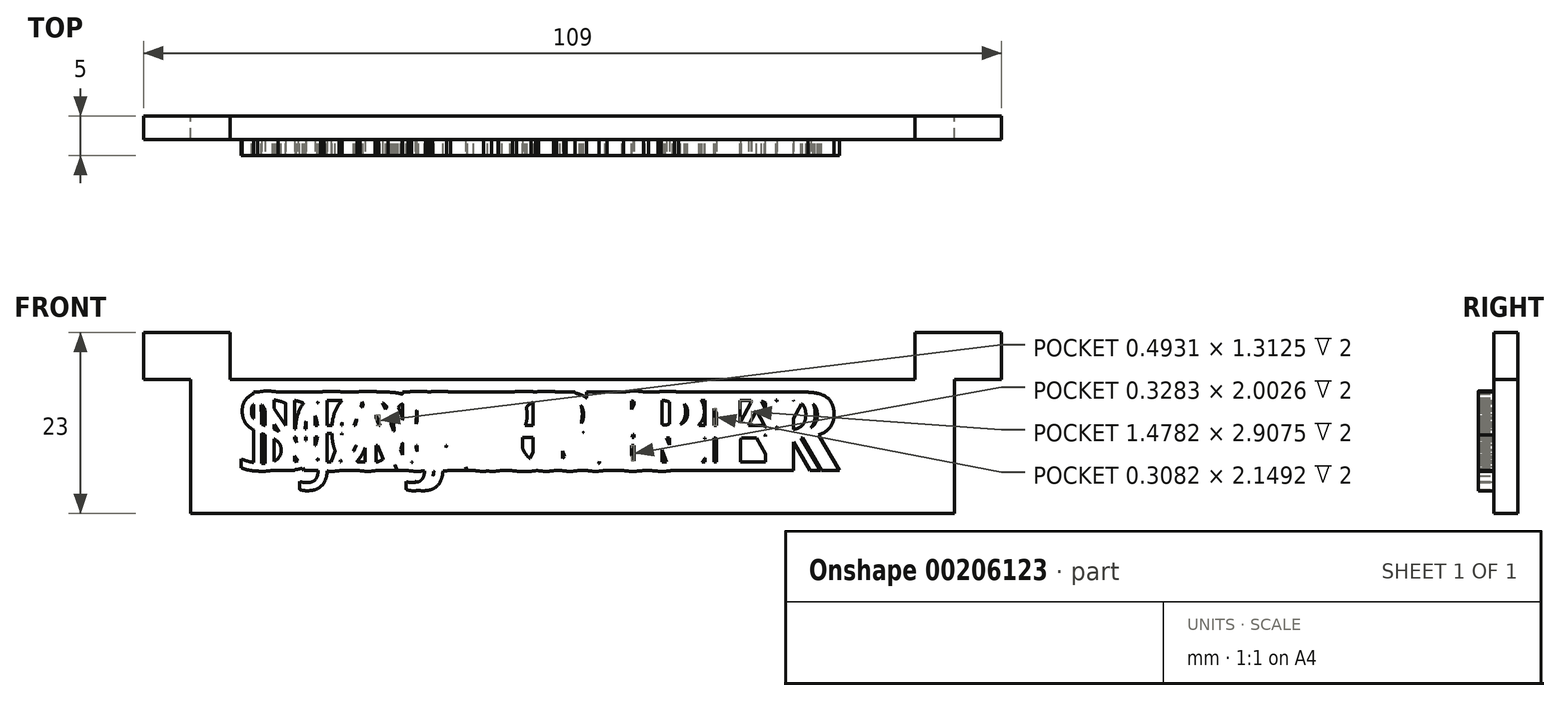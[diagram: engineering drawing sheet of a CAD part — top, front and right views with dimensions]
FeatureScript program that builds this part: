
annotation { "Feature Type Name" : "Feature", "Feature Type Description" : "" }
export const myFeature = defineFeature(function(context is Context, id is Id, definition is map)
    precondition{}
    {
        {
            var Q0;
            Q0=qCreatedBy(makeId("Front.planeOp"),FACE);
            var sketch = newSketch(context, id + "F0", { "sketchPlane" : qUnion([Q0])});
            skLineSegment(sketch, "E0.bottom", {"start": v(-51.5, 23) * mm, "end": v(-40.5, 23) * mm});
            skLineSegment(sketch, "E0.top", {"start": v(-45.5, 0) * mm, "end": v(51.5, 0) * mm});
            skLineSegment(sketch, "E0.left", {"start": v(-51.5, 23) * mm, "end": v(-51.5, 17) * mm});
            skLineSegment(sketch, "E0.right", {"start": v(57.5, 23) * mm, "end": v(57.5, 17) * mm});
            skLineSegment(sketch, "E1.top", {"start": v(-51.5, 17) * mm, "end": v(-45.5, 17) * mm});
            skLineSegment(sketch, "E1.right", {"start": v(-45.5, 0) * mm, "end": v(-45.5, 17) * mm});
            skLineSegment(sketch, "E2.bottom", {"start": v(-51.5, 23) * mm, "end": v(-40.5, 23) * mm, "construction": true});
            skLineSegment(sketch, "E2.top", {"start": v(-51.5, 17) * mm, "end": v(-40.5, 17) * mm, "construction": true});
            skLineSegment(sketch, "E2.left", {"start": v(-51.5, 23) * mm, "end": v(-51.5, 17) * mm, "construction": true});
            skLineSegment(sketch, "E2.right", {"start": v(-40.5, 23) * mm, "end": v(-40.5, 17) * mm, "construction": true});
            skLineSegment(sketch, "E3.top", {"start": v(-40.5, 17) * mm, "end": v(46.5, 17) * mm});
            skLineSegment(sketch, "E3.left", {"start": v(-40.5, 23) * mm, "end": v(-40.5, 17) * mm});
            skLineSegment(sketch, "E3.right", {"start": v(46.5, 23) * mm, "end": v(46.5, 17) * mm});
            skLineSegment(sketch, "E4.top", {"start": v(57.5, 17) * mm, "end": v(51.5, 17) * mm});
            skLineSegment(sketch, "E4.right", {"start": v(51.5, 0) * mm, "end": v(51.5, 17) * mm});
            skLineSegment(sketch, "E5.trimOffspring", {"start": v(46.5, 23) * mm, "end": v(57.5, 23) * mm});
            skSolve(sketch);
        }
        {
            var Q0;
            Q0=makeQuery(id+"F0.imprint","IMPRINT",FACE,{"disambiguationData":[TD([[makeQuery(id+"F0.imprint","IMPRINT",EDGE,{"derivedFrom":sQuery(id+"F0.wireOp",EDGE,"E0.bottom")}),-1.0]])]});
            extrude(context, id + "F1", {"entities" : qUnion([Q0]), "depth" : 3 * mm});
        }
        {
            var Q0;
            Q0=makeQuery(id+"F1.opExtrude","CAP_FACE",FACE,{"disambiguationData":[OSD([sQuery(id+"F0.wireOp",EDGE,"E0.bottom"),sQuery(id+"F0.wireOp",EDGE,"E0.top"),sQuery(id+"F0.wireOp",EDGE,"E0.left"),sQuery(id+"F0.wireOp",EDGE,"E0.right"),sQuery(id+"F0.wireOp",EDGE,"E1.top"),sQuery(id+"F0.wireOp",EDGE,"E1.right"),sQuery(id+"F0.wireOp",EDGE,"E3.top"),sQuery(id+"F0.wireOp",EDGE,"E3.left"),sQuery(id+"F0.wireOp",EDGE,"E3.right"),sQuery(id+"F0.wireOp",EDGE,"E4.top"),sQuery(id+"F0.wireOp",EDGE,"E4.right"),sQuery(id+"F0.wireOp",EDGE,"E5.trimOffspring")])],"isStart":false});
            var sketch = newSketch(context, id + "F2", { "sketchPlane" : qUnion([Q0])});
            skLineSegment(sketch, "E6.0", {"start": v(-45.5, 3.5) * mm, "end": v(-42, 3.5) * mm, "construction": true});
            skLineSegment(sketch, "E7.0", {"start": v(-42, 15.5) * mm, "end": v(48, 15.5) * mm, "construction": true});
            skLineSegment(sketch, "E8.0", {"start": v(-42, 0) * mm, "end": v(-42, 15.5) * mm, "construction": true});
            skText(sketch, "E9", { "text": "JANUARY", "fontName": "OpenSans-Regular.ttf"});
            skLineSegment(sketch, "E10.top", {"start": v(-45.5, 0) * mm, "end": v(-42, 0) * mm, "construction": true});
            skLineSegment(sketch, "E10.left", {"start": v(-45.5, 3.5) * mm, "end": v(-45.5, 0) * mm, "construction": true});
            skLineSegment(sketch, "E10.right", {"start": v(-42, 3.5) * mm, "end": v(-42, 0) * mm, "construction": true});
            skLineSegment(sketch, "E11.0", {"start": v(48, 0) * mm, "end": v(48, 17) * mm, "construction": true});
            skPoint(sketch, "E12.orphan", {"position": v(48, 15.5) * mm});
            skPoint(sketch, "E13.end.orphan", {"position": v(3, 0) * mm});
            skLineSegment(sketch, "E14", {"start": v(3, 17) * mm, "end": v(3, 0) * mm, "construction": true});
            const initialGuessF2  = {"E9": [-0.0306, 0.0055, 1, 0, 0.01]};
            skSetInitialGuess(sketch, initialGuessF2);
            skSolve(sketch);
        }
        {
            var Q0;
            Q0=makeQuery(id+"F2.imprint","IMPRINT",FACE,{"disambiguationData":[TD([[makeQuery(id+"F2.imprint","IMPRINT",EDGE,{"derivedFrom":sQuery(id+"F2.wireOp",EDGE,"E9.sketch_text.stroke-0")}),-1.0]])]});
            var Q1;
            Q1=makeQuery(id+"F2.imprint","IMPRINT",FACE,{"disambiguationData":[TD([[makeQuery(id+"F2.imprint","IMPRINT",EDGE,{"derivedFrom":sQuery(id+"F2.wireOp",EDGE,"E9.sketch_text.stroke-10")}),-1.0]])]});
            var Q2;
            Q2=makeQuery(id+"F2.imprint","IMPRINT",FACE,{"disambiguationData":[TD([[makeQuery(id+"F2.imprint","IMPRINT",EDGE,{"derivedFrom":sQuery(id+"F2.wireOp",EDGE,"E9.sketch_text.stroke-23")}),-1.0]])]});
            var Q3;
            Q3=makeQuery(id+"F2.imprint","IMPRINT",FACE,{"disambiguationData":[TD([[makeQuery(id+"F2.imprint","IMPRINT",EDGE,{"derivedFrom":sQuery(id+"F2.wireOp",EDGE,"E9.sketch_text.stroke-38")}),-1.0]])]});
            var Q4;
            Q4=makeQuery(id+"F2.imprint","IMPRINT",FACE,{"disambiguationData":[TD([[makeQuery(id+"F2.imprint","IMPRINT",EDGE,{"derivedFrom":sQuery(id+"F2.wireOp",EDGE,"E9.sketch_text.stroke-52")}),-1.0]])]});
            var Q5;
            Q5=makeQuery(id+"F2.imprint","IMPRINT",FACE,{"disambiguationData":[TD([[makeQuery(id+"F2.imprint","IMPRINT",EDGE,{"derivedFrom":sQuery(id+"F2.wireOp",EDGE,"E9.sketch_text.stroke-65")}),-1.0]])]});
            var Q6;
            Q6=makeQuery(id+"F2.imprint","IMPRINT",FACE,{"disambiguationData":[TD([[makeQuery(id+"F2.imprint","IMPRINT",EDGE,{"derivedFrom":sQuery(id+"F2.wireOp",EDGE,"E9.sketch_text.stroke-83")}),-1.0]])]});
            extrude(context, id + "F3", {"entities" : qUnion([Q0, Q1, Q2, Q3, Q4, Q5, Q6]), "operationType" : NewBodyOperationType.ADD, "depth" : 2 * mm});
        }
        {
            var Q0;
            Q0=qSketchRegion(id+"F0",true);
            extrude(context, id + "F4", {"entities" : qUnion([Q0]), "depth" : 3 * mm});
        }
        {
            var Q0;
            Q0=makeQuery(id+"F4.opExtrude","CAP_FACE",FACE,{"disambiguationData":[OSD([sQuery(id+"F0.wireOp",EDGE,"E0.bottom"),sQuery(id+"F0.wireOp",EDGE,"E0.top"),sQuery(id+"F0.wireOp",EDGE,"E0.left"),sQuery(id+"F0.wireOp",EDGE,"E0.right"),sQuery(id+"F0.wireOp",EDGE,"E1.top"),sQuery(id+"F0.wireOp",EDGE,"E1.right"),sQuery(id+"F0.wireOp",EDGE,"E3.top"),sQuery(id+"F0.wireOp",EDGE,"E3.left"),sQuery(id+"F0.wireOp",EDGE,"E3.right"),sQuery(id+"F0.wireOp",EDGE,"E4.top"),sQuery(id+"F0.wireOp",EDGE,"E4.right"),sQuery(id+"F0.wireOp",EDGE,"E5.trimOffspring")])],"isStart":false});
            var sketch = newSketch(context, id + "F5", { "sketchPlane" : qUnion([Q0])});
            skText(sketch, "E15", { "text": "FEBRUARY", "fontName": "OpenSans-Regular.ttf"});
            skPoint(sketch, "E16.orphan", {"position": v(48.71, 15.5) * mm});
            skPoint(sketch, "E17.end.orphan", {"position": v(-0.5, 0) * mm});
            skPoint(sketch, "E18.orphan", {"position": v(-42.71, 15.5) * mm});
            skLineSegment(sketch, "E19.0", {"start": v(-43.5, 15.5) * mm, "end": v(49.5, 15.5) * mm, "construction": true});
            skPoint(sketch, "E20.start.orphan", {"position": v(3, 17) * mm});
            const initialGuessF5  = {"E15": [-0.03482, 0.0055, 1, 0, 0.01]};
            skSetInitialGuess(sketch, initialGuessF5);
            skSolve(sketch);
        }
        {
            var Q0;
            Q0=makeQuery(id+"F5.imprint","IMPRINT",FACE,{"disambiguationData":[TD([[makeQuery(id+"F5.imprint","IMPRINT",EDGE,{"derivedFrom":sQuery(id+"F5.wireOp",EDGE,"E15.sketch_text.stroke-0")}),-1.0]])]});
            var Q1;
            Q1=makeQuery(id+"F5.imprint","IMPRINT",FACE,{"disambiguationData":[TD([[makeQuery(id+"F5.imprint","IMPRINT",EDGE,{"derivedFrom":sQuery(id+"F5.wireOp",EDGE,"E15.sketch_text.stroke-10")}),-1.0]])]});
            var Q2;
            Q2=makeQuery(id+"F5.imprint","IMPRINT",FACE,{"disambiguationData":[TD([[makeQuery(id+"F5.imprint","IMPRINT",EDGE,{"derivedFrom":sQuery(id+"F5.wireOp",EDGE,"E15.sketch_text.stroke-22")}),-1.0]])]});
            var Q3;
            Q3=makeQuery(id+"F5.imprint","IMPRINT",FACE,{"disambiguationData":[TD([[makeQuery(id+"F5.imprint","IMPRINT",EDGE,{"derivedFrom":sQuery(id+"F5.wireOp",EDGE,"E15.sketch_text.stroke-47")}),-1.0]])]});
            var Q4;
            Q4=makeQuery(id+"F5.imprint","IMPRINT",FACE,{"disambiguationData":[TD([[makeQuery(id+"F5.imprint","IMPRINT",EDGE,{"derivedFrom":sQuery(id+"F5.wireOp",EDGE,"E15.sketch_text.stroke-65")}),-1.0]])]});
            var Q5;
            Q5=makeQuery(id+"F5.imprint","IMPRINT",FACE,{"disambiguationData":[TD([[makeQuery(id+"F5.imprint","IMPRINT",EDGE,{"derivedFrom":sQuery(id+"F5.wireOp",EDGE,"E15.sketch_text.stroke-79")}),-1.0]])]});
            var Q6;
            Q6=makeQuery(id+"F5.imprint","IMPRINT",FACE,{"disambiguationData":[TD([[makeQuery(id+"F5.imprint","IMPRINT",EDGE,{"derivedFrom":sQuery(id+"F5.wireOp",EDGE,"E15.sketch_text.stroke-92")}),-1.0]])]});
            var Q7;
            Q7=makeQuery(id+"F5.imprint","IMPRINT",FACE,{"disambiguationData":[TD([[makeQuery(id+"F5.imprint","IMPRINT",EDGE,{"derivedFrom":sQuery(id+"F5.wireOp",EDGE,"E15.sketch_text.stroke-110")}),-1.0]])]});
            extrude(context, id + "F6", {"entities" : qUnion([Q0, Q1, Q2, Q3, Q4, Q5, Q6, Q7]), "operationType" : NewBodyOperationType.ADD, "depth" : 2 * mm});
        }
        {
            var Q0;
            Q0=makeQuery(id+"F0.imprint","IMPRINT",FACE,{"disambiguationData":[TD([[makeQuery(id+"F0.imprint","IMPRINT",EDGE,{"derivedFrom":sQuery(id+"F0.wireOp",EDGE,"E0.bottom")}),-1.0]])]});
            extrude(context, id + "F7", {"entities" : qUnion([Q0]), "depth" : 3 * mm});
        }
        {
            var Q0;
            Q0=makeQuery(id+"F7.opExtrude","CAP_FACE",FACE,{"disambiguationData":[OSD([sQuery(id+"F0.wireOp",EDGE,"E0.bottom"),sQuery(id+"F0.wireOp",EDGE,"E0.top"),sQuery(id+"F0.wireOp",EDGE,"E0.left"),sQuery(id+"F0.wireOp",EDGE,"E0.right"),sQuery(id+"F0.wireOp",EDGE,"E1.top"),sQuery(id+"F0.wireOp",EDGE,"E1.right"),sQuery(id+"F0.wireOp",EDGE,"E3.top"),sQuery(id+"F0.wireOp",EDGE,"E3.left"),sQuery(id+"F0.wireOp",EDGE,"E3.right"),sQuery(id+"F0.wireOp",EDGE,"E4.top"),sQuery(id+"F0.wireOp",EDGE,"E4.right"),sQuery(id+"F0.wireOp",EDGE,"E5.trimOffspring")])],"isStart":false});
            var sketch = newSketch(context, id + "F8", { "sketchPlane" : qUnion([Q0])});
            skText(sketch, "E21", { "text": "MARCH", "fontName": "OpenSans-Regular.ttf"});
            skPoint(sketch, "E22.orphan", {"position": v(38.63, 15.5) * mm});
            skPoint(sketch, "E23.end.orphan", {"position": v(0, -12.7) * mm});
            skPoint(sketch, "E24.orphan", {"position": v(-32.63, 15.5) * mm});
            skPoint(sketch, "E25.start.orphan", {"position": v(0, 4.3) * mm});
            skLineSegment(sketch, "E26.0", {"start": v(-43.5, 15.5) * mm, "end": v(49.5, 15.5) * mm, "construction": true});
            const initialGuessF8  = {"E21": [-0.02473, 0.0055, 1, 0, 0.01]};
            skSetInitialGuess(sketch, initialGuessF8);
            skSolve(sketch);
        }
        {
            var Q0;
            Q0=makeQuery(id+"F8.imprint","IMPRINT",FACE,{"disambiguationData":[TD([[makeQuery(id+"F8.imprint","IMPRINT",EDGE,{"derivedFrom":sQuery(id+"F8.wireOp",EDGE,"E21.sketch_text.stroke-0")}),-1.0]])]});
            var Q1;
            Q1=makeQuery(id+"F8.imprint","IMPRINT",FACE,{"disambiguationData":[TD([[makeQuery(id+"F8.imprint","IMPRINT",EDGE,{"derivedFrom":sQuery(id+"F8.wireOp",EDGE,"E21.sketch_text.stroke-18")}),-1.0]])]});
            var Q2;
            Q2=makeQuery(id+"F8.imprint","IMPRINT",FACE,{"disambiguationData":[TD([[makeQuery(id+"F8.imprint","IMPRINT",EDGE,{"derivedFrom":sQuery(id+"F8.wireOp",EDGE,"E21.sketch_text.stroke-31")}),-1.0]])]});
            var Q3;
            Q3=makeQuery(id+"F8.imprint","IMPRINT",FACE,{"disambiguationData":[TD([[makeQuery(id+"F8.imprint","IMPRINT",EDGE,{"derivedFrom":sQuery(id+"F8.wireOp",EDGE,"E21.sketch_text.stroke-49")}),-1.0]])]});
            var Q4;
            Q4=makeQuery(id+"F8.imprint","IMPRINT",FACE,{"disambiguationData":[TD([[makeQuery(id+"F8.imprint","IMPRINT",EDGE,{"derivedFrom":sQuery(id+"F8.wireOp",EDGE,"E21.sketch_text.stroke-64")}),-1.0]])]});
            extrude(context, id + "F9", {"entities" : qUnion([Q0, Q1, Q2, Q3, Q4]), "operationType" : NewBodyOperationType.ADD, "depth" : 2 * mm});
        }
        {
            var Q0;
            Q0=makeQuery(id+"F0.imprint","IMPRINT",FACE,{"disambiguationData":[TD([[makeQuery(id+"F0.imprint","IMPRINT",EDGE,{"derivedFrom":sQuery(id+"F0.wireOp",EDGE,"E0.bottom")}),-1.0]])]});
            extrude(context, id + "F10", {"entities" : qUnion([Q0]), "depth" : 3 * mm});
        }
        {
            var Q0;
            Q0=makeQuery(id+"F10.opExtrude","CAP_FACE",FACE,{"disambiguationData":[OSD([sQuery(id+"F0.wireOp",EDGE,"E0.bottom"),sQuery(id+"F0.wireOp",EDGE,"E0.top"),sQuery(id+"F0.wireOp",EDGE,"E0.left"),sQuery(id+"F0.wireOp",EDGE,"E0.right"),sQuery(id+"F0.wireOp",EDGE,"E1.top"),sQuery(id+"F0.wireOp",EDGE,"E1.right"),sQuery(id+"F0.wireOp",EDGE,"E3.top"),sQuery(id+"F0.wireOp",EDGE,"E3.left"),sQuery(id+"F0.wireOp",EDGE,"E3.right"),sQuery(id+"F0.wireOp",EDGE,"E4.top"),sQuery(id+"F0.wireOp",EDGE,"E4.right"),sQuery(id+"F0.wireOp",EDGE,"E5.trimOffspring")])],"isStart":false});
            var sketch = newSketch(context, id + "F11", { "sketchPlane" : qUnion([Q0])});
            skText(sketch, "E27", { "text": "APRIL", "fontName": "OpenSans-Regular.ttf"});
            skPoint(sketch, "E28.orphan", {"position": v(33.1, 15.5) * mm});
            skPoint(sketch, "E29.end.orphan", {"position": v(0.3, -20.32) * mm});
            skPoint(sketch, "E30.orphan", {"position": v(-27.1, 15.5) * mm});
            skPoint(sketch, "E31.start.orphan", {"position": v(0.3, -3.32) * mm});
            skLineSegment(sketch, "E32.0", {"start": v(-43.5, 15.5) * mm, "end": v(49.5, 15.5) * mm});
            const initialGuessF11  = {"E27": [-0.0192, 0.0055, 1, 0, 0.01]};
            skSetInitialGuess(sketch, initialGuessF11);
            skSolve(sketch);
        }
        {
            var Q0;
            Q0=makeQuery(id+"F11.imprint","IMPRINT",FACE,{"disambiguationData":[TD([[makeQuery(id+"F11.imprint","IMPRINT",EDGE,{"derivedFrom":sQuery(id+"F11.wireOp",EDGE,"E27.sketch_text.stroke-0")}),-1.0]])]});
            var Q1;
            Q1=makeQuery(id+"F11.imprint","IMPRINT",FACE,{"disambiguationData":[TD([[makeQuery(id+"F11.imprint","IMPRINT",EDGE,{"derivedFrom":sQuery(id+"F11.wireOp",EDGE,"E27.sketch_text.stroke-13")}),-1.0]])]});
            var Q2;
            Q2=makeQuery(id+"F11.imprint","IMPRINT",FACE,{"disambiguationData":[TD([[makeQuery(id+"F11.imprint","IMPRINT",EDGE,{"derivedFrom":sQuery(id+"F11.wireOp",EDGE,"E27.sketch_text.stroke-28")}),-1.0]])]});
            var Q3;
            Q3=makeQuery(id+"F11.imprint","IMPRINT",FACE,{"disambiguationData":[TD([[makeQuery(id+"F11.imprint","IMPRINT",EDGE,{"derivedFrom":sQuery(id+"F11.wireOp",EDGE,"E27.sketch_text.stroke-46")}),-1.0]])]});
            var Q4;
            Q4=makeQuery(id+"F11.imprint","IMPRINT",FACE,{"disambiguationData":[TD([[makeQuery(id+"F11.imprint","IMPRINT",EDGE,{"derivedFrom":sQuery(id+"F11.wireOp",EDGE,"E27.sketch_text.stroke-50")}),-1.0]])]});
            extrude(context, id + "F12", {"entities" : qUnion([Q0, Q1, Q2, Q3, Q4]), "operationType" : NewBodyOperationType.ADD, "depth" : 2 * mm});
        }
        {
            var Q0;
            Q0=makeQuery(id+"F0.imprint","IMPRINT",FACE,{"disambiguationData":[TD([[makeQuery(id+"F0.imprint","IMPRINT",EDGE,{"derivedFrom":sQuery(id+"F0.wireOp",EDGE,"E0.bottom")}),-1.0]])]});
            extrude(context, id + "F13", {"entities" : qUnion([Q0]), "depth" : 3 * mm});
        }
        {
            var Q0;
            Q0=makeQuery(id+"F13.opExtrude","CAP_FACE",FACE,{"disambiguationData":[OSD([sQuery(id+"F0.wireOp",EDGE,"E0.bottom"),sQuery(id+"F0.wireOp",EDGE,"E0.top"),sQuery(id+"F0.wireOp",EDGE,"E0.left"),sQuery(id+"F0.wireOp",EDGE,"E0.right"),sQuery(id+"F0.wireOp",EDGE,"E1.top"),sQuery(id+"F0.wireOp",EDGE,"E1.right"),sQuery(id+"F0.wireOp",EDGE,"E3.top"),sQuery(id+"F0.wireOp",EDGE,"E3.left"),sQuery(id+"F0.wireOp",EDGE,"E3.right"),sQuery(id+"F0.wireOp",EDGE,"E4.top"),sQuery(id+"F0.wireOp",EDGE,"E4.right"),sQuery(id+"F0.wireOp",EDGE,"E5.trimOffspring")])],"isStart":false});
            var sketch = newSketch(context, id + "F14", { "sketchPlane" : qUnion([Q0])});
            skText(sketch, "E33", { "text": "MAY", "fontName": "OpenSans-Regular.ttf"});
            skPoint(sketch, "E34.orphan", {"position": v(29.4, 15.5) * mm});
            skPoint(sketch, "E35.end.orphan", {"position": v(0.48, -24.9) * mm});
            skPoint(sketch, "E36.orphan", {"position": v(-23.4, 15.5) * mm});
            skPoint(sketch, "E37.start.orphan", {"position": v(0.48, -7.9) * mm});
            skLineSegment(sketch, "E38.0", {"start": v(-36.3, 15.5) * mm, "end": v(42.3, 15.5) * mm});
            skLineSegment(sketch, "E39.0", {"start": v(-43.5, 15.5) * mm, "end": v(49.5, 15.5) * mm});
            const initialGuessF14  = {"E33": [-0.0155, 0.0055, 1, 0, 0.01]};
            skSetInitialGuess(sketch, initialGuessF14);
            skSolve(sketch);
        }
        {
            var Q0;
            Q0=makeQuery(id+"F0.imprint","IMPRINT",FACE,{"disambiguationData":[TD([[makeQuery(id+"F0.imprint","IMPRINT",EDGE,{"derivedFrom":sQuery(id+"F0.wireOp",EDGE,"E0.bottom")}),-1.0]])]});
            extrude(context, id + "F15", {"entities" : qUnion([Q0]), "depth" : 3 * mm});
        }
        {
            var Q0;
            Q0=makeQuery(id+"F15.opExtrude","CAP_FACE",FACE,{"disambiguationData":[OSD([sQuery(id+"F0.wireOp",EDGE,"E0.bottom"),sQuery(id+"F0.wireOp",EDGE,"E0.top"),sQuery(id+"F0.wireOp",EDGE,"E0.left"),sQuery(id+"F0.wireOp",EDGE,"E0.right"),sQuery(id+"F0.wireOp",EDGE,"E1.top"),sQuery(id+"F0.wireOp",EDGE,"E1.right"),sQuery(id+"F0.wireOp",EDGE,"E3.top"),sQuery(id+"F0.wireOp",EDGE,"E3.left"),sQuery(id+"F0.wireOp",EDGE,"E3.right"),sQuery(id+"F0.wireOp",EDGE,"E4.top"),sQuery(id+"F0.wireOp",EDGE,"E4.right"),sQuery(id+"F0.wireOp",EDGE,"E5.trimOffspring")])],"isStart":false});
            var sketch = newSketch(context, id + "F16", { "sketchPlane" : qUnion([Q0])});
            skText(sketch, "E40", { "text": "JUNE", "fontName": "OpenSans-Regular.ttf"});
            skPoint(sketch, "E41.orphan", {"position": v(30.97, 15.5) * mm});
            skPoint(sketch, "E42.end.orphan", {"position": v(0.65, -29.76) * mm});
            skPoint(sketch, "E43.orphan", {"position": v(-24.97, 15.5) * mm});
            skPoint(sketch, "E44.start.orphan", {"position": v(0.65, -12.76) * mm});
            skLineSegment(sketch, "E45.0", {"start": v(-37.88, 15.5) * mm, "end": v(43.88, 15.5) * mm});
            skLineSegment(sketch, "E46.0", {"start": v(-41.58, 15.5) * mm, "end": v(47.58, 15.5) * mm});
            skLineSegment(sketch, "E47.0", {"start": v(-43.5, 15.5) * mm, "end": v(49.5, 15.5) * mm});
            const initialGuessF16  = {"E40": [-0.01708, 0.0055, 1, 0, 0.01]};
            skSetInitialGuess(sketch, initialGuessF16);
            skSolve(sketch);
        }
        {
            var Q0;
            Q0=makeQuery(id+"F0.imprint","IMPRINT",FACE,{"disambiguationData":[TD([[makeQuery(id+"F0.imprint","IMPRINT",EDGE,{"derivedFrom":sQuery(id+"F0.wireOp",EDGE,"E0.bottom")}),-1.0]])]});
            extrude(context, id + "F17", {"entities" : qUnion([Q0]), "depth" : 3 * mm});
        }
        {
            var Q0;
            Q0=makeQuery(id+"F17.opExtrude","CAP_FACE",FACE,{"disambiguationData":[OSD([sQuery(id+"F0.wireOp",EDGE,"E0.bottom"),sQuery(id+"F0.wireOp",EDGE,"E0.top"),sQuery(id+"F0.wireOp",EDGE,"E0.left"),sQuery(id+"F0.wireOp",EDGE,"E0.right"),sQuery(id+"F0.wireOp",EDGE,"E1.top"),sQuery(id+"F0.wireOp",EDGE,"E1.right"),sQuery(id+"F0.wireOp",EDGE,"E3.top"),sQuery(id+"F0.wireOp",EDGE,"E3.left"),sQuery(id+"F0.wireOp",EDGE,"E3.right"),sQuery(id+"F0.wireOp",EDGE,"E4.top"),sQuery(id+"F0.wireOp",EDGE,"E4.right"),sQuery(id+"F0.wireOp",EDGE,"E5.trimOffspring")])],"isStart":false});
            var sketch = newSketch(context, id + "F18", { "sketchPlane" : qUnion([Q0])});
            skText(sketch, "E48", { "text": "JULY", "fontName": "OpenSans-Regular.ttf"});
            skPoint(sketch, "E49.orphan", {"position": v(29.79, 15.5) * mm});
            skPoint(sketch, "E50.end.orphan", {"position": v(0.82, -34.76) * mm});
            skPoint(sketch, "E51.orphan", {"position": v(-23.79, 15.5) * mm});
            skPoint(sketch, "E52.start.orphan", {"position": v(0.82, -17.76) * mm});
            skLineSegment(sketch, "E53.0", {"start": v(-36.7, 15.5) * mm, "end": v(42.7, 15.5) * mm});
            skLineSegment(sketch, "E54.0", {"start": v(-40.4, 15.5) * mm, "end": v(46.4, 15.5) * mm});
            skLineSegment(sketch, "E55.0", {"start": v(-38.81, 15.5) * mm, "end": v(44.81, 15.5) * mm});
            skLineSegment(sketch, "E56.0", {"start": v(-43.5, 15.5) * mm, "end": v(49.5, 15.5) * mm});
            const initialGuessF18  = {"E48": [-0.0159, 0.0055, 1, 0, 0.01]};
            skSetInitialGuess(sketch, initialGuessF18);
            skSolve(sketch);
        }
        {
            var Q0;
            Q0=makeQuery(id+"F0.imprint","IMPRINT",FACE,{"disambiguationData":[TD([[makeQuery(id+"F0.imprint","IMPRINT",EDGE,{"derivedFrom":sQuery(id+"F0.wireOp",EDGE,"E0.bottom")}),-1.0]])]});
            extrude(context, id + "F19", {"entities" : qUnion([Q0]), "depth" : 3 * mm});
        }
        {
            var Q0;
            Q0=makeQuery(id+"F19.opExtrude","CAP_FACE",FACE,{"disambiguationData":[OSD([sQuery(id+"F0.wireOp",EDGE,"E0.bottom"),sQuery(id+"F0.wireOp",EDGE,"E0.top"),sQuery(id+"F0.wireOp",EDGE,"E0.left"),sQuery(id+"F0.wireOp",EDGE,"E0.right"),sQuery(id+"F0.wireOp",EDGE,"E1.top"),sQuery(id+"F0.wireOp",EDGE,"E1.right"),sQuery(id+"F0.wireOp",EDGE,"E3.top"),sQuery(id+"F0.wireOp",EDGE,"E3.left"),sQuery(id+"F0.wireOp",EDGE,"E3.right"),sQuery(id+"F0.wireOp",EDGE,"E4.top"),sQuery(id+"F0.wireOp",EDGE,"E4.right"),sQuery(id+"F0.wireOp",EDGE,"E5.trimOffspring")])],"isStart":false});
            var sketch = newSketch(context, id + "F20", { "sketchPlane" : qUnion([Q0])});
            skText(sketch, "E57", { "text": "AUGUST", "fontName": "OpenSans-Regular.ttf"});
            skPoint(sketch, "E58.orphan", {"position": v(42, 15.5) * mm});
            skPoint(sketch, "E59.end.orphan", {"position": v(1, -39.82) * mm});
            skPoint(sketch, "E60.orphan", {"position": v(-36, 15.5) * mm});
            skPoint(sketch, "E61.start.orphan", {"position": v(1, -22.82) * mm});
            skLineSegment(sketch, "E62.0", {"start": v(-48.9, 15.5) * mm, "end": v(54.9, 15.5) * mm});
            skLineSegment(sketch, "E63.0", {"start": v(-52.6, 15.5) * mm, "end": v(58.6, 15.5) * mm});
            skLineSegment(sketch, "E64.0", {"start": v(-51.02, 15.5) * mm, "end": v(57.02, 15.5) * mm});
            skLineSegment(sketch, "E65.0", {"start": v(-52.2, 15.5) * mm, "end": v(58.2, 15.5) * mm});
            skLineSegment(sketch, "E66.0", {"start": v(-43.5, 15.5) * mm, "end": v(49.5, 15.5) * mm});
            const initialGuessF20  = {"E57": [-0.0281, 0.0055, 1, 0, 0.01]};
            skSetInitialGuess(sketch, initialGuessF20);
            skSolve(sketch);
        }
        {
            var Q0;
            Q0=makeQuery(id+"F0.imprint","IMPRINT",FACE,{"disambiguationData":[TD([[makeQuery(id+"F0.imprint","IMPRINT",EDGE,{"derivedFrom":sQuery(id+"F0.wireOp",EDGE,"E0.bottom")}),-1.0]])]});
            extrude(context, id + "F21", {"entities" : qUnion([Q0]), "depth" : 3 * mm});
        }
        {
            var Q0;
            Q0=makeQuery(id+"F21.opExtrude","CAP_FACE",FACE,{"disambiguationData":[OSD([sQuery(id+"F0.wireOp",EDGE,"E0.bottom"),sQuery(id+"F0.wireOp",EDGE,"E0.top"),sQuery(id+"F0.wireOp",EDGE,"E0.left"),sQuery(id+"F0.wireOp",EDGE,"E0.right"),sQuery(id+"F0.wireOp",EDGE,"E1.top"),sQuery(id+"F0.wireOp",EDGE,"E1.right"),sQuery(id+"F0.wireOp",EDGE,"E3.top"),sQuery(id+"F0.wireOp",EDGE,"E3.left"),sQuery(id+"F0.wireOp",EDGE,"E3.right"),sQuery(id+"F0.wireOp",EDGE,"E4.top"),sQuery(id+"F0.wireOp",EDGE,"E4.right"),sQuery(id+"F0.wireOp",EDGE,"E5.trimOffspring")])],"isStart":false});
            var sketch = newSketch(context, id + "F22", { "sketchPlane" : qUnion([Q0])});
            skText(sketch, "E67", { "text": "SEPTEMBER", "fontName": "OpenSans-Regular.ttf"});
            skPoint(sketch, "E68.orphan", {"position": v(53.2, 15.5) * mm});
            skPoint(sketch, "E69.end.orphan", {"position": v(1.16, -44.91) * mm});
            skPoint(sketch, "E70.orphan", {"position": v(-47.2, 15.5) * mm});
            skPoint(sketch, "E71.start.orphan", {"position": v(1.16, -27.91) * mm});
            const initialGuessF22  = {"E67": [-0.03981, 0.0055, 1, 0, 0.01]};
            skSetInitialGuess(sketch, initialGuessF22);
            skSolve(sketch);
        }
        {
            var Q0;
            Q0=makeQuery(id+"F0.imprint","IMPRINT",FACE,{"disambiguationData":[TD([[makeQuery(id+"F0.imprint","IMPRINT",EDGE,{"derivedFrom":sQuery(id+"F0.wireOp",EDGE,"E0.bottom")}),-1.0]])]});
            extrude(context, id + "F23", {"entities" : qUnion([Q0]), "depth" : 3 * mm});
        }
        {
            var Q0;
            Q0=makeQuery(id+"F23.opExtrude","CAP_FACE",FACE,{"disambiguationData":[OSD([sQuery(id+"F0.wireOp",EDGE,"E0.bottom"),sQuery(id+"F0.wireOp",EDGE,"E0.top"),sQuery(id+"F0.wireOp",EDGE,"E0.left"),sQuery(id+"F0.wireOp",EDGE,"E0.right"),sQuery(id+"F0.wireOp",EDGE,"E1.top"),sQuery(id+"F0.wireOp",EDGE,"E1.right"),sQuery(id+"F0.wireOp",EDGE,"E3.top"),sQuery(id+"F0.wireOp",EDGE,"E3.left"),sQuery(id+"F0.wireOp",EDGE,"E3.right"),sQuery(id+"F0.wireOp",EDGE,"E4.top"),sQuery(id+"F0.wireOp",EDGE,"E4.right"),sQuery(id+"F0.wireOp",EDGE,"E5.trimOffspring")])],"isStart":false});
            var sketch = newSketch(context, id + "F24", { "sketchPlane" : qUnion([Q0])});
            skText(sketch, "E72", { "text": "OCTOBER", "fontName": "OpenSans-Regular.ttf"});
            skPoint(sketch, "E73.orphan", {"position": v(46.42, 15.5) * mm});
            skPoint(sketch, "E74.end.orphan", {"position": v(1.08, -34.46) * mm});
            skPoint(sketch, "E75.orphan", {"position": v(-40.42, 15.5) * mm});
            skPoint(sketch, "E76.start.orphan", {"position": v(1.08, -17.46) * mm});
            skLineSegment(sketch, "E77.0", {"start": v(-42.5, 15.5) * mm, "end": v(48.5, 15.5) * mm});
            const initialGuessF24  = {"E72": [-0.03303, 0.0055, 1, 0, 0.01]};
            skSetInitialGuess(sketch, initialGuessF24);
            skSolve(sketch);
        }
        {
            var Q0;
            Q0=makeQuery(id+"F0.imprint","IMPRINT",FACE,{"disambiguationData":[TD([[makeQuery(id+"F0.imprint","IMPRINT",EDGE,{"derivedFrom":sQuery(id+"F0.wireOp",EDGE,"E0.bottom")}),-1.0]])]});
            extrude(context, id + "F25", {"entities" : qUnion([Q0]), "depth" : 3 * mm});
        }
        {
            var Q0;
            Q0=makeQuery(id+"F25.opExtrude","CAP_FACE",FACE,{"disambiguationData":[OSD([sQuery(id+"F0.wireOp",EDGE,"E0.bottom"),sQuery(id+"F0.wireOp",EDGE,"E0.top"),sQuery(id+"F0.wireOp",EDGE,"E0.left"),sQuery(id+"F0.wireOp",EDGE,"E0.right"),sQuery(id+"F0.wireOp",EDGE,"E1.top"),sQuery(id+"F0.wireOp",EDGE,"E1.right"),sQuery(id+"F0.wireOp",EDGE,"E3.top"),sQuery(id+"F0.wireOp",EDGE,"E3.left"),sQuery(id+"F0.wireOp",EDGE,"E3.right"),sQuery(id+"F0.wireOp",EDGE,"E4.top"),sQuery(id+"F0.wireOp",EDGE,"E4.right"),sQuery(id+"F0.wireOp",EDGE,"E5.trimOffspring")])],"isStart":false});
            var sketch = newSketch(context, id + "F26", { "sketchPlane" : qUnion([Q0])});
            skText(sketch, "E78", { "text": "NOVEMBER", "fontName": "OpenSans-Regular.ttf"});
            skPoint(sketch, "E79.orphan", {"position": v(52.29, 15.5) * mm});
            skPoint(sketch, "E80.end.orphan", {"position": v(1.08, -34.46) * mm});
            skPoint(sketch, "E81.orphan", {"position": v(-46.29, 15.5) * mm});
            skPoint(sketch, "E82.start.orphan", {"position": v(1.08, -17.46) * mm});
            skLineSegment(sketch, "E83.0", {"start": v(-42.5, 15.5) * mm, "end": v(48.5, 15.5) * mm});
            const initialGuessF26  = {"E78": [-0.0389, 0.0055, 1, 0, 0.01]};
            skSetInitialGuess(sketch, initialGuessF26);
            skSolve(sketch);
        }
        {
            var Q0;
            Q0=makeQuery(id+"F0.imprint","IMPRINT",FACE,{"disambiguationData":[TD([[makeQuery(id+"F0.imprint","IMPRINT",EDGE,{"derivedFrom":sQuery(id+"F0.wireOp",EDGE,"E0.bottom")}),-1.0]])]});
            extrude(context, id + "F27", {"entities" : qUnion([Q0]), "depth" : 3 * mm});
        }
        {
            var Q0;
            Q0=makeQuery(id+"F27.opExtrude","CAP_FACE",FACE,{"disambiguationData":[OSD([sQuery(id+"F0.wireOp",EDGE,"E0.bottom"),sQuery(id+"F0.wireOp",EDGE,"E0.top"),sQuery(id+"F0.wireOp",EDGE,"E0.left"),sQuery(id+"F0.wireOp",EDGE,"E0.right"),sQuery(id+"F0.wireOp",EDGE,"E1.top"),sQuery(id+"F0.wireOp",EDGE,"E1.right"),sQuery(id+"F0.wireOp",EDGE,"E3.top"),sQuery(id+"F0.wireOp",EDGE,"E3.left"),sQuery(id+"F0.wireOp",EDGE,"E3.right"),sQuery(id+"F0.wireOp",EDGE,"E4.top"),sQuery(id+"F0.wireOp",EDGE,"E4.right"),sQuery(id+"F0.wireOp",EDGE,"E5.trimOffspring")])],"isStart":false});
            var sketch = newSketch(context, id + "F28", { "sketchPlane" : qUnion([Q0])});
            skText(sketch, "E84", { "text": "DECEMBER", "fontName": "OpenSans-Regular.ttf"});
            skPoint(sketch, "E85.orphan", {"position": v(50.82, 15.5) * mm});
            skPoint(sketch, "E86.end.orphan", {"position": v(1.08, -34.46) * mm});
            skPoint(sketch, "E87.orphan", {"position": v(-44.82, 15.5) * mm});
            skPoint(sketch, "E88.start.orphan", {"position": v(1.08, -17.46) * mm});
            skLineSegment(sketch, "E89.0", {"start": v(-42.5, 15.5) * mm, "end": v(48.5, 15.5) * mm});
            const initialGuessF28  = {"E84": [-0.03742, 0.0055, 1, 0, 0.01]};
            skSetInitialGuess(sketch, initialGuessF28);
            skSolve(sketch);
        }
        {
            var Q0;
            Q0=makeQuery(id+"F28.imprint","IMPRINT",FACE,{"disambiguationData":[TD([[makeQuery(id+"F28.imprint","IMPRINT",EDGE,{"derivedFrom":sQuery(id+"F28.wireOp",EDGE,"E84.sketch_text.stroke-0")}),-1.0]])]});
            var Q1;
            Q1=makeQuery(id+"F28.imprint","IMPRINT",FACE,{"disambiguationData":[TD([[makeQuery(id+"F28.imprint","IMPRINT",EDGE,{"derivedFrom":sQuery(id+"F28.wireOp",EDGE,"E84.sketch_text.stroke-14")}),-1.0]])]});
            var Q2;
            Q2=makeQuery(id+"F28.imprint","IMPRINT",FACE,{"disambiguationData":[TD([[makeQuery(id+"F28.imprint","IMPRINT",EDGE,{"derivedFrom":sQuery(id+"F28.wireOp",EDGE,"E84.sketch_text.stroke-26")}),-1.0]])]});
            var Q3;
            Q3=makeQuery(id+"F28.imprint","IMPRINT",FACE,{"disambiguationData":[TD([[makeQuery(id+"F28.imprint","IMPRINT",EDGE,{"derivedFrom":sQuery(id+"F28.wireOp",EDGE,"E84.sketch_text.stroke-41")}),-1.0]])]});
            var Q4;
            Q4=makeQuery(id+"F28.imprint","IMPRINT",FACE,{"disambiguationData":[TD([[makeQuery(id+"F28.imprint","IMPRINT",EDGE,{"derivedFrom":sQuery(id+"F28.wireOp",EDGE,"E84.sketch_text.stroke-53")}),-1.0]])]});
            var Q5;
            Q5=makeQuery(id+"F28.imprint","IMPRINT",FACE,{"disambiguationData":[TD([[makeQuery(id+"F28.imprint","IMPRINT",EDGE,{"derivedFrom":sQuery(id+"F28.wireOp",EDGE,"E84.sketch_text.stroke-71")}),-1.0]])]});
            var Q6;
            Q6=makeQuery(id+"F28.imprint","IMPRINT",FACE,{"disambiguationData":[TD([[makeQuery(id+"F28.imprint","IMPRINT",EDGE,{"derivedFrom":sQuery(id+"F28.wireOp",EDGE,"E84.sketch_text.stroke-96")}),-1.0]])]});
            var Q7;
            Q7=makeQuery(id+"F28.imprint","IMPRINT",FACE,{"disambiguationData":[TD([[makeQuery(id+"F28.imprint","IMPRINT",EDGE,{"derivedFrom":sQuery(id+"F28.wireOp",EDGE,"E84.sketch_text.stroke-108")}),-1.0]])]});
            extrude(context, id + "F29", {"entities" : qUnion([Q0, Q1, Q2, Q3, Q4, Q5, Q6, Q7]), "operationType" : NewBodyOperationType.ADD, "depth" : 2 * mm});
        }
        {
            var Q0;
            Q0=makeQuery(id+"F26.imprint","IMPRINT",FACE,{"disambiguationData":[TD([[makeQuery(id+"F26.imprint","IMPRINT",EDGE,{"derivedFrom":sQuery(id+"F26.wireOp",EDGE,"E78.sketch_text.stroke-0")}),-1.0]])]});
            var Q1;
            Q1=makeQuery(id+"F26.imprint","IMPRINT",FACE,{"disambiguationData":[TD([[makeQuery(id+"F26.imprint","IMPRINT",EDGE,{"derivedFrom":sQuery(id+"F26.wireOp",EDGE,"E78.sketch_text.stroke-15")}),-1.0]])]});
            var Q2;
            Q2=makeQuery(id+"F26.imprint","IMPRINT",FACE,{"disambiguationData":[TD([[makeQuery(id+"F26.imprint","IMPRINT",EDGE,{"derivedFrom":sQuery(id+"F26.wireOp",EDGE,"E78.sketch_text.stroke-31")}),-1.0]])]});
            var Q3;
            Q3=makeQuery(id+"F26.imprint","IMPRINT",FACE,{"disambiguationData":[TD([[makeQuery(id+"F26.imprint","IMPRINT",EDGE,{"derivedFrom":sQuery(id+"F26.wireOp",EDGE,"E78.sketch_text.stroke-40")}),-1.0]])]});
            var Q4;
            Q4=makeQuery(id+"F26.imprint","IMPRINT",FACE,{"disambiguationData":[TD([[makeQuery(id+"F26.imprint","IMPRINT",EDGE,{"derivedFrom":sQuery(id+"F26.wireOp",EDGE,"E78.sketch_text.stroke-52")}),-1.0]])]});
            var Q5;
            Q5=makeQuery(id+"F26.imprint","IMPRINT",FACE,{"disambiguationData":[TD([[makeQuery(id+"F26.imprint","IMPRINT",EDGE,{"derivedFrom":sQuery(id+"F26.wireOp",EDGE,"E78.sketch_text.stroke-70")}),-1.0]])]});
            var Q6;
            Q6=makeQuery(id+"F26.imprint","IMPRINT",FACE,{"disambiguationData":[TD([[makeQuery(id+"F26.imprint","IMPRINT",EDGE,{"derivedFrom":sQuery(id+"F26.wireOp",EDGE,"E78.sketch_text.stroke-95")}),-1.0]])]});
            var Q7;
            Q7=makeQuery(id+"F26.imprint","IMPRINT",FACE,{"disambiguationData":[TD([[makeQuery(id+"F26.imprint","IMPRINT",EDGE,{"derivedFrom":sQuery(id+"F26.wireOp",EDGE,"E78.sketch_text.stroke-107")}),-1.0]])]});
            extrude(context, id + "F30", {"entities" : qUnion([Q0, Q1, Q2, Q3, Q4, Q5, Q6, Q7]), "operationType" : NewBodyOperationType.ADD, "depth" : 2 * mm});
        }
        {
            var Q0;
            Q0=makeQuery(id+"F24.imprint","IMPRINT",FACE,{"disambiguationData":[TD([[makeQuery(id+"F24.imprint","IMPRINT",EDGE,{"derivedFrom":sQuery(id+"F24.wireOp",EDGE,"E72.sketch_text.stroke-0")}),-1.0]])]});
            var Q1;
            Q1=makeQuery(id+"F24.imprint","IMPRINT",FACE,{"disambiguationData":[TD([[makeQuery(id+"F24.imprint","IMPRINT",EDGE,{"derivedFrom":sQuery(id+"F24.wireOp",EDGE,"E72.sketch_text.stroke-16")}),-1.0]])]});
            var Q2;
            Q2=makeQuery(id+"F24.imprint","IMPRINT",FACE,{"disambiguationData":[TD([[makeQuery(id+"F24.imprint","IMPRINT",EDGE,{"derivedFrom":sQuery(id+"F24.wireOp",EDGE,"E72.sketch_text.stroke-31")}),-1.0]])]});
            var Q3;
            Q3=makeQuery(id+"F24.imprint","IMPRINT",FACE,{"disambiguationData":[TD([[makeQuery(id+"F24.imprint","IMPRINT",EDGE,{"derivedFrom":sQuery(id+"F24.wireOp",EDGE,"E72.sketch_text.stroke-39")}),-1.0]])]});
            var Q4;
            Q4=makeQuery(id+"F24.imprint","IMPRINT",FACE,{"disambiguationData":[TD([[makeQuery(id+"F24.imprint","IMPRINT",EDGE,{"derivedFrom":sQuery(id+"F24.wireOp",EDGE,"E72.sketch_text.stroke-55")}),-1.0]])]});
            var Q5;
            Q5=makeQuery(id+"F24.imprint","IMPRINT",FACE,{"disambiguationData":[TD([[makeQuery(id+"F24.imprint","IMPRINT",EDGE,{"derivedFrom":sQuery(id+"F24.wireOp",EDGE,"E72.sketch_text.stroke-80")}),-1.0]])]});
            var Q6;
            Q6=makeQuery(id+"F24.imprint","IMPRINT",FACE,{"disambiguationData":[TD([[makeQuery(id+"F24.imprint","IMPRINT",EDGE,{"derivedFrom":sQuery(id+"F24.wireOp",EDGE,"E72.sketch_text.stroke-92")}),-1.0]])]});
            extrude(context, id + "F31", {"entities" : qUnion([Q0, Q1, Q2, Q3, Q4, Q5, Q6]), "operationType" : NewBodyOperationType.ADD, "depth" : 2 * mm});
        }
        {
            var Q0;
            Q0=makeQuery(id+"F22.imprint","IMPRINT",FACE,{"disambiguationData":[TD([[makeQuery(id+"F22.imprint","IMPRINT",EDGE,{"derivedFrom":sQuery(id+"F22.wireOp",EDGE,"E67.sketch_text.stroke-0")}),-1.0]])]});
            var Q1;
            Q1=makeQuery(id+"F22.imprint","IMPRINT",FACE,{"disambiguationData":[TD([[makeQuery(id+"F22.imprint","IMPRINT",EDGE,{"derivedFrom":sQuery(id+"F22.wireOp",EDGE,"E67.sketch_text.stroke-25")}),-1.0]])]});
            var Q2;
            Q2=makeQuery(id+"F22.imprint","IMPRINT",FACE,{"disambiguationData":[TD([[makeQuery(id+"F22.imprint","IMPRINT",EDGE,{"derivedFrom":sQuery(id+"F22.wireOp",EDGE,"E67.sketch_text.stroke-37")}),-1.0]])]});
            var Q3;
            Q3=makeQuery(id+"F22.imprint","IMPRINT",FACE,{"disambiguationData":[TD([[makeQuery(id+"F22.imprint","IMPRINT",EDGE,{"derivedFrom":sQuery(id+"F22.wireOp",EDGE,"E67.sketch_text.stroke-52")}),-1.0]])]});
            var Q4;
            Q4=makeQuery(id+"F22.imprint","IMPRINT",FACE,{"disambiguationData":[TD([[makeQuery(id+"F22.imprint","IMPRINT",EDGE,{"derivedFrom":sQuery(id+"F22.wireOp",EDGE,"E67.sketch_text.stroke-60")}),-1.0]])]});
            var Q5;
            Q5=makeQuery(id+"F22.imprint","IMPRINT",FACE,{"disambiguationData":[TD([[makeQuery(id+"F22.imprint","IMPRINT",EDGE,{"derivedFrom":sQuery(id+"F22.wireOp",EDGE,"E67.sketch_text.stroke-72")}),-1.0]])]});
            var Q6;
            Q6=makeQuery(id+"F22.imprint","IMPRINT",FACE,{"disambiguationData":[TD([[makeQuery(id+"F22.imprint","IMPRINT",EDGE,{"derivedFrom":sQuery(id+"F22.wireOp",EDGE,"E67.sketch_text.stroke-90")}),-1.0]])]});
            var Q7;
            Q7=makeQuery(id+"F22.imprint","IMPRINT",FACE,{"disambiguationData":[TD([[makeQuery(id+"F22.imprint","IMPRINT",EDGE,{"derivedFrom":sQuery(id+"F22.wireOp",EDGE,"E67.sketch_text.stroke-115")}),-1.0]])]});
            var Q8;
            Q8=makeQuery(id+"F22.imprint","IMPRINT",FACE,{"disambiguationData":[TD([[makeQuery(id+"F22.imprint","IMPRINT",EDGE,{"derivedFrom":sQuery(id+"F22.wireOp",EDGE,"E67.sketch_text.stroke-127")}),-1.0]])]});
            extrude(context, id + "F32", {"entities" : qUnion([Q0, Q1, Q2, Q3, Q4, Q5, Q6, Q7, Q8]), "operationType" : NewBodyOperationType.ADD, "depth" : 2 * mm});
        }
        {
            var Q0;
            Q0=makeQuery(id+"F20.imprint","IMPRINT",FACE,{"disambiguationData":[TD([[makeQuery(id+"F20.imprint","IMPRINT",EDGE,{"derivedFrom":sQuery(id+"F20.wireOp",EDGE,"E57.sketch_text.stroke-0")}),-1.0]])]});
            var Q1;
            Q1=makeQuery(id+"F20.imprint","IMPRINT",FACE,{"disambiguationData":[TD([[makeQuery(id+"F20.imprint","IMPRINT",EDGE,{"derivedFrom":sQuery(id+"F20.wireOp",EDGE,"E57.sketch_text.stroke-13")}),-1.0]])]});
            var Q2;
            Q2=makeQuery(id+"F20.imprint","IMPRINT",FACE,{"disambiguationData":[TD([[makeQuery(id+"F20.imprint","IMPRINT",EDGE,{"derivedFrom":sQuery(id+"F20.wireOp",EDGE,"E57.sketch_text.stroke-27")}),-1.0]])]});
            var Q3;
            Q3=makeQuery(id+"F20.imprint","IMPRINT",FACE,{"disambiguationData":[TD([[makeQuery(id+"F20.imprint","IMPRINT",EDGE,{"derivedFrom":sQuery(id+"F20.wireOp",EDGE,"E57.sketch_text.stroke-47")}),-1.0]])]});
            var Q4;
            Q4=makeQuery(id+"F20.imprint","IMPRINT",FACE,{"disambiguationData":[TD([[makeQuery(id+"F20.imprint","IMPRINT",EDGE,{"derivedFrom":sQuery(id+"F20.wireOp",EDGE,"E57.sketch_text.stroke-61")}),-1.0]])]});
            var Q5;
            Q5=makeQuery(id+"F20.imprint","IMPRINT",FACE,{"disambiguationData":[TD([[makeQuery(id+"F20.imprint","IMPRINT",EDGE,{"derivedFrom":sQuery(id+"F20.wireOp",EDGE,"E57.sketch_text.stroke-86")}),-1.0]])]});
            extrude(context, id + "F33", {"entities" : qUnion([Q0, Q1, Q2, Q3, Q4, Q5]), "operationType" : NewBodyOperationType.ADD, "depth" : 2 * mm});
        }
        {
            var Q0;
            Q0=makeQuery(id+"F18.imprint","IMPRINT",FACE,{"disambiguationData":[TD([[makeQuery(id+"F18.imprint","IMPRINT",EDGE,{"derivedFrom":sQuery(id+"F18.wireOp",EDGE,"E48.sketch_text.stroke-0")}),-1.0]])]});
            var Q1;
            Q1=makeQuery(id+"F18.imprint","IMPRINT",FACE,{"disambiguationData":[TD([[makeQuery(id+"F18.imprint","IMPRINT",EDGE,{"derivedFrom":sQuery(id+"F18.wireOp",EDGE,"E48.sketch_text.stroke-10")}),-1.0]])]});
            var Q2;
            Q2=makeQuery(id+"F18.imprint","IMPRINT",FACE,{"disambiguationData":[TD([[makeQuery(id+"F18.imprint","IMPRINT",EDGE,{"derivedFrom":sQuery(id+"F18.wireOp",EDGE,"E48.sketch_text.stroke-24")}),-1.0]])]});
            var Q3;
            Q3=makeQuery(id+"F18.imprint","IMPRINT",FACE,{"disambiguationData":[TD([[makeQuery(id+"F18.imprint","IMPRINT",EDGE,{"derivedFrom":sQuery(id+"F18.wireOp",EDGE,"E48.sketch_text.stroke-30")}),-1.0]])]});
            extrude(context, id + "F34", {"entities" : qUnion([Q0, Q1, Q2, Q3]), "operationType" : NewBodyOperationType.ADD, "depth" : 2 * mm});
        }
        {
            var Q0;
            Q0=makeQuery(id+"F16.imprint","IMPRINT",FACE,{"disambiguationData":[TD([[makeQuery(id+"F16.imprint","IMPRINT",EDGE,{"derivedFrom":sQuery(id+"F16.wireOp",EDGE,"E40.sketch_text.stroke-0")}),-1.0]])]});
            var Q1;
            Q1=makeQuery(id+"F16.imprint","IMPRINT",FACE,{"disambiguationData":[TD([[makeQuery(id+"F16.imprint","IMPRINT",EDGE,{"derivedFrom":sQuery(id+"F16.wireOp",EDGE,"E40.sketch_text.stroke-10")}),-1.0]])]});
            var Q2;
            Q2=makeQuery(id+"F16.imprint","IMPRINT",FACE,{"disambiguationData":[TD([[makeQuery(id+"F16.imprint","IMPRINT",EDGE,{"derivedFrom":sQuery(id+"F16.wireOp",EDGE,"E40.sketch_text.stroke-24")}),-1.0]])]});
            var Q3;
            Q3=makeQuery(id+"F16.imprint","IMPRINT",FACE,{"disambiguationData":[TD([[makeQuery(id+"F16.imprint","IMPRINT",EDGE,{"derivedFrom":sQuery(id+"F16.wireOp",EDGE,"E40.sketch_text.stroke-39")}),-1.0]])]});
            extrude(context, id + "F35", {"entities" : qUnion([Q0, Q1, Q2, Q3]), "operationType" : NewBodyOperationType.ADD, "depth" : 2 * mm});
        }
        {
            var Q0;
            Q0=makeQuery(id+"F14.imprint","IMPRINT",FACE,{"disambiguationData":[TD([[makeQuery(id+"F14.imprint","IMPRINT",EDGE,{"derivedFrom":sQuery(id+"F14.wireOp",EDGE,"E33.sketch_text.stroke-0")}),-1.0]])]});
            var Q1;
            Q1=makeQuery(id+"F14.imprint","IMPRINT",FACE,{"disambiguationData":[TD([[makeQuery(id+"F14.imprint","IMPRINT",EDGE,{"derivedFrom":sQuery(id+"F14.wireOp",EDGE,"E33.sketch_text.stroke-18")}),-1.0]])]});
            var Q2;
            Q2=makeQuery(id+"F14.imprint","IMPRINT",FACE,{"disambiguationData":[TD([[makeQuery(id+"F14.imprint","IMPRINT",EDGE,{"derivedFrom":sQuery(id+"F14.wireOp",EDGE,"E33.sketch_text.stroke-31")}),-1.0]])]});
            extrude(context, id + "F36", {"entities" : qUnion([Q0, Q1, Q2]), "operationType" : NewBodyOperationType.ADD, "depth" : 2 * mm});
        }
        {
            var Q0;
            Q0=makeQuery(id+"F0.imprint","IMPRINT",FACE,{"disambiguationData":[TD([[makeQuery(id+"F0.imprint","IMPRINT",EDGE,{"derivedFrom":sQuery(id+"F0.wireOp",EDGE,"E0.bottom")}),-1.0]])]});
            extrude(context, id + "F37", {"entities" : qUnion([Q0]), "depth" : 3 * mm});
        }
    });
